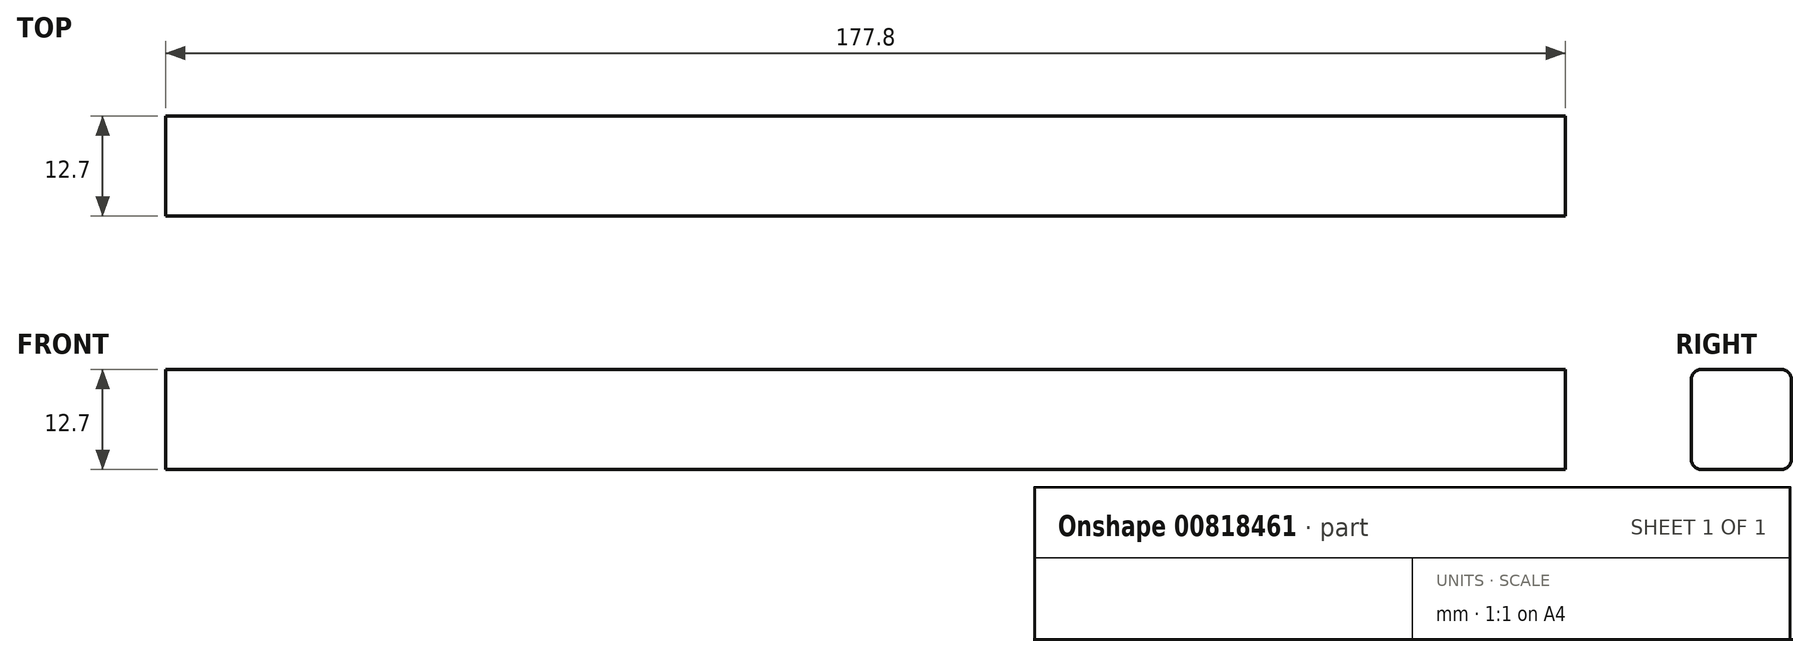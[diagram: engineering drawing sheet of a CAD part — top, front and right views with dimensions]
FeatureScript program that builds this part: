
annotation { "Feature Type Name" : "Feature", "Feature Type Description" : "" }
export const myFeature = defineFeature(function(context is Context, id is Id, definition is map)
    precondition{}
    {
        {
            var Q0;
            Q0=qCreatedBy(makeId("Top.planeOp"),FACE);
            var sketch = newSketch(context, id + "F0", { "sketchPlane" : qUnion([Q0])});
            skLineSegment(sketch, "E0.bottom", {"start": v(-88.9, 6.35) * mm, "end": v(88.9, 6.35) * mm});
            skLineSegment(sketch, "E0.top", {"start": v(-88.9, -6.35) * mm, "end": v(88.9, -6.35) * mm});
            skLineSegment(sketch, "E0.left", {"start": v(-88.9, 6.35) * mm, "end": v(-88.9, -6.35) * mm});
            skLineSegment(sketch, "E0.right", {"start": v(88.9, 6.35) * mm, "end": v(88.9, -6.35) * mm});
            skPoint(sketch, "E0.middle", {"position": v(0, 0) * mm});
            skSolve(sketch);
        }
        {
            var Q0;
            Q0=makeQuery(id+"F0.imprint","IMPRINT",FACE,{"disambiguationData":[TD([[makeQuery(id+"F0.imprint","IMPRINT",EDGE,{"derivedFrom":sQuery(id+"F0.wireOp",EDGE,"E0.bottom")}),-1.0]])]});
            extrude(context, id + "F1", {"entities" : qUnion([Q0]), "depth" : 12.7 * mm, "offsetDistance" : 25.4 * mm});
        }
        {
            var Q0;
            Q0=makeQuery(id+"F1.opExtrude","CAP_EDGE",EDGE,{"disambiguationData":[OSD([sQuery(id+"F0.wireOp",EDGE,"E0.bottom")])],"isStart":true});
            var Q1;
            Q1=makeQuery(id+"F1.opExtrude","CAP_EDGE",EDGE,{"disambiguationData":[OSD([sQuery(id+"F0.wireOp",EDGE,"E0.top")])],"isStart":false});
            var Q2;
            Q2=makeQuery(id+"F1.opExtrude","CAP_EDGE",EDGE,{"disambiguationData":[OSD([sQuery(id+"F0.wireOp",EDGE,"E0.top")])],"isStart":true});
            var Q3;
            Q3=makeQuery(id+"F1.opExtrude","CAP_EDGE",EDGE,{"disambiguationData":[OSD([sQuery(id+"F0.wireOp",EDGE,"E0.bottom")])],"isStart":false});
            fillet(context, id + "F2", {"entities" : qUnion([Q0, Q1, Q2, Q3]), "radius" : 1.27 * mm, "tangentPropagation" : true, "allowEdgeOverflow" : false});
        }
    });
